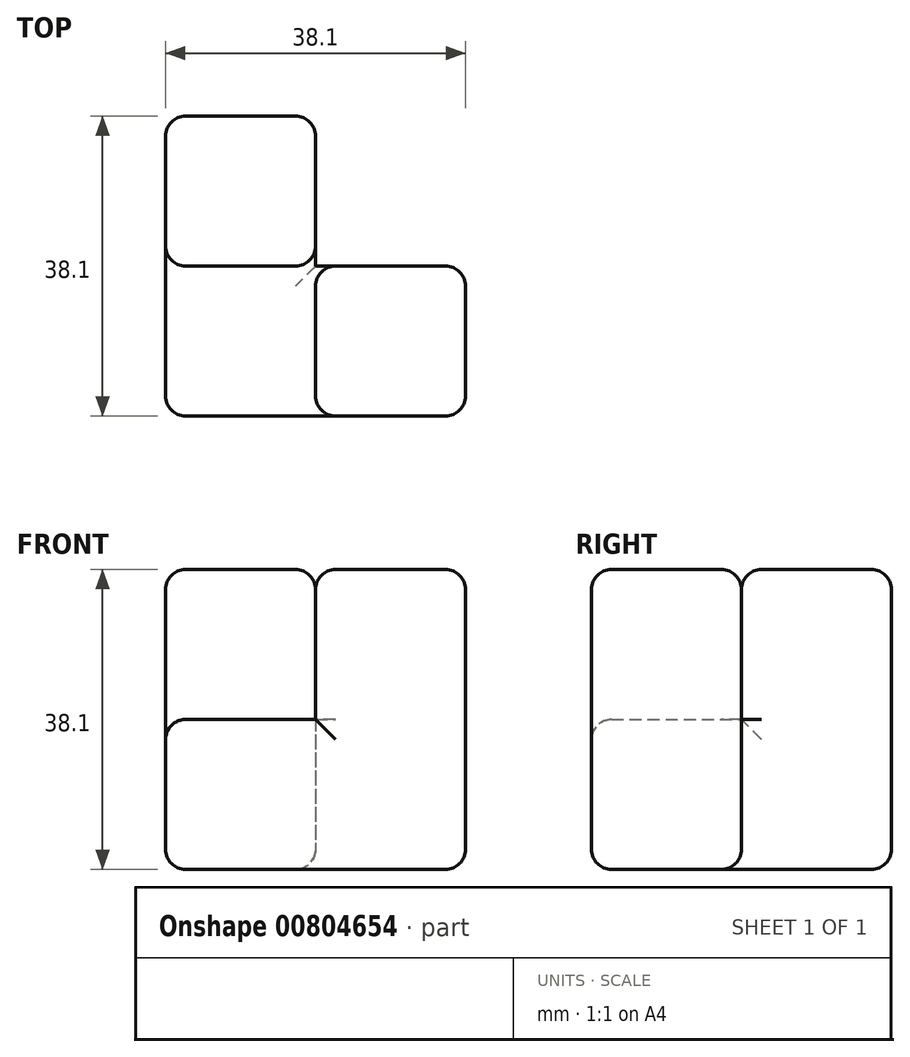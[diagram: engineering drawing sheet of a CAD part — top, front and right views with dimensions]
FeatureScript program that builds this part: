
annotation { "Feature Type Name" : "Feature", "Feature Type Description" : "" }
export const myFeature = defineFeature(function(context is Context, id is Id, definition is map)
    precondition{}
    {
        {
            var Q0;
            Q0=qCreatedBy(makeId("Top.planeOp"),FACE);
            var sketch = newSketch(context, id + "F0", { "sketchPlane" : qUnion([Q0])});
            skLineSegment(sketch, "E0", {"start": v(0, 0) * mm, "end": v(0, 38.1) * mm});
            skLineSegment(sketch, "E1", {"start": v(0, 38.1) * mm, "end": v(19.05, 38.1) * mm});
            skLineSegment(sketch, "E2", {"start": v(19.05, 38.1) * mm, "end": v(19.05, 19.05) * mm});
            skLineSegment(sketch, "E3", {"start": v(19.05, 19.05) * mm, "end": v(38.1, 19.05) * mm});
            skLineSegment(sketch, "E4", {"start": v(38.1, 19.05) * mm, "end": v(38.1, 0) * mm});
            skLineSegment(sketch, "E5", {"start": v(38.1, 0) * mm, "end": v(0, 0) * mm});
            skSolve(sketch);
        }
        {
            var Q0;
            Q0=qSketchRegion(id+"F0",true);
            extrude(context, id + "F1", {"entities" : qUnion([Q0]), "depth" : 19.05 * mm, "offsetDistance" : 25.4 * mm});
        }
        {
            var Q0;
            Q0=makeQuery(id+"F1.opExtrude","CAP_FACE",FACE,{"disambiguationData":[OSD([sQuery(id+"F0.wireOp",EDGE,"E0"),sQuery(id+"F0.wireOp",EDGE,"E1"),sQuery(id+"F0.wireOp",EDGE,"E2"),sQuery(id+"F0.wireOp",EDGE,"E3"),sQuery(id+"F0.wireOp",EDGE,"E4"),sQuery(id+"F0.wireOp",EDGE,"E5")])],"isStart":false});
            var sketch = newSketch(context, id + "F2", { "sketchPlane" : qUnion([Q0])});
            skLineSegment(sketch, "E6.bottom", {"start": v(0, 38.1) * mm, "end": v(19.05, 38.1) * mm});
            skLineSegment(sketch, "E6.top", {"start": v(0, 19.05) * mm, "end": v(19.05, 19.05) * mm});
            skLineSegment(sketch, "E6.left", {"start": v(0, 38.1) * mm, "end": v(0, 19.05) * mm});
            skLineSegment(sketch, "E6.right", {"start": v(19.05, 38.1) * mm, "end": v(19.05, 19.05) * mm});
            skLineSegment(sketch, "E7.bottom", {"start": v(38.1, 0) * mm, "end": v(19.05, 0) * mm});
            skLineSegment(sketch, "E7.top", {"start": v(38.1, 19.05) * mm, "end": v(19.05, 19.05) * mm});
            skLineSegment(sketch, "E7.left", {"start": v(38.1, 0) * mm, "end": v(38.1, 19.05) * mm});
            skLineSegment(sketch, "E7.right", {"start": v(19.05, 0) * mm, "end": v(19.05, 19.05) * mm});
            skSolve(sketch);
        }
        {
            var Q0;
            Q0=makeQuery(id+"F2.imprint","IMPRINT",FACE,{"disambiguationData":[TD([[makeQuery(id+"F2.imprint","IMPRINT",EDGE,{"derivedFrom":sQuery(id+"F2.wireOp",EDGE,"E7.bottom")}),-1.0]])]});
            extrude(context, id + "F3", {"entities" : qUnion([Q0]), "operationType" : NewBodyOperationType.ADD, "depth" : 19.05 * mm, "offsetDistance" : 25.4 * mm});
        }
        {
            var Q0;
            Q0=makeQuery(id+"F3.opExtrude","SWEPT_EDGE",EDGE,{"disambiguationData":[OSD([sQuery(id+"F2.wireOp",EDGE,"E6.top"),sQuery(id+"F2.wireOp",EDGE,"E6.right"),sQuery(id+"F2.wireOp",EDGE,"E7.top"),sQuery(id+"F2.wireOp",EDGE,"E7.right")])]});
            fillet(context, id + "F4", {"entities" : qUnion([Q0]), "radius" : 2.54 * mm, "tangentPropagation" : true, "allowEdgeOverflow" : false});
        }
        {
            var Q0;
            Q0=makeQuery(id+"F2.imprint","IMPRINT",FACE,{"disambiguationData":[TD([[makeQuery(id+"F2.imprint","IMPRINT",EDGE,{"derivedFrom":sQuery(id+"F2.wireOp",EDGE,"E6.bottom")}),-1.0]])]});
            extrude(context, id + "F5", {"entities" : qUnion([Q0]), "operationType" : NewBodyOperationType.ADD, "depth" : 19.05 * mm, "offsetDistance" : 25.4 * mm});
        }
        {
            var Q0;
            Q0=makeQuery(id+"F3.boolean.opBoolean","MERGE",FACE,{"derivedFrom":[makeQuery(id+"F1.opExtrude","SWEPT_FACE",FACE,{"disambiguationData":[OSD([sQuery(id+"F0.wireOp",EDGE,"E4")])]}),makeQuery(id+"F3.opExtrude","SWEPT_FACE",FACE,{"disambiguationData":[OSD([sQuery(id+"F2.wireOp",EDGE,"E7.left")])]})]});
            var Q1;
            Q1=makeQuery(id+"F5.boolean.opBoolean","MERGE",FACE,{"derivedFrom":[makeQuery(id+"F1.opExtrude","SWEPT_FACE",FACE,{"disambiguationData":[OSD([sQuery(id+"F0.wireOp",EDGE,"E1")])]}),makeQuery(id+"F5.opExtrude","SWEPT_FACE",FACE,{"disambiguationData":[OSD([sQuery(id+"F2.wireOp",EDGE,"E6.bottom")])]})]});
            var Q2;
            Q2=makeQuery(id+"F5.opExtrude","CAP_FACE",FACE,{"disambiguationData":[OSD([sQuery(id+"F2.wireOp",EDGE,"E6.bottom"),sQuery(id+"F2.wireOp",EDGE,"E6.top"),sQuery(id+"F2.wireOp",EDGE,"E6.left"),sQuery(id+"F2.wireOp",EDGE,"E6.right")])],"isStart":false});
            var Q3;
            Q3=makeQuery(id+"F3.opExtrude","CAP_FACE",FACE,{"disambiguationData":[OSD([sQuery(id+"F2.wireOp",EDGE,"E7.bottom"),sQuery(id+"F2.wireOp",EDGE,"E7.top"),sQuery(id+"F2.wireOp",EDGE,"E7.left"),sQuery(id+"F2.wireOp",EDGE,"E7.right")])],"isStart":false});
            var Q4;
            Q4=makeQuery(id+"F5.boolean.opBoolean","MERGE",FACE,{"derivedFrom":[makeQuery(id+"F1.opExtrude","SWEPT_FACE",FACE,{"disambiguationData":[OSD([sQuery(id+"F0.wireOp",EDGE,"E0")])]}),makeQuery(id+"F5.opExtrude","SWEPT_FACE",FACE,{"disambiguationData":[OSD([sQuery(id+"F2.wireOp",EDGE,"E6.left")])]})]});
            var Q5;
            Q5=makeQuery(id+"F3.boolean.opBoolean","MERGE",FACE,{"derivedFrom":[makeQuery(id+"F1.opExtrude","SWEPT_FACE",FACE,{"disambiguationData":[OSD([sQuery(id+"F0.wireOp",EDGE,"E5")])]}),makeQuery(id+"F3.opExtrude","SWEPT_FACE",FACE,{"disambiguationData":[OSD([sQuery(id+"F2.wireOp",EDGE,"E7.bottom")])]})]});
            var Q6;
            Q6=makeQuery(id+"F1.opExtrude","CAP_FACE",FACE,{"disambiguationData":[OSD([sQuery(id+"F0.wireOp",EDGE,"E0"),sQuery(id+"F0.wireOp",EDGE,"E1"),sQuery(id+"F0.wireOp",EDGE,"E2"),sQuery(id+"F0.wireOp",EDGE,"E3"),sQuery(id+"F0.wireOp",EDGE,"E4"),sQuery(id+"F0.wireOp",EDGE,"E5")])],"isStart":true});
            var Q7;
            Q7=makeQuery(id+"F5.opExtrude","SWEPT_EDGE",EDGE,{"disambiguationData":[OSD([sQuery(id+"F2.wireOp",EDGE,"E6.top"),sQuery(id+"F2.wireOp",EDGE,"E6.right"),sQuery(id+"F2.wireOp",EDGE,"E7.top"),sQuery(id+"F2.wireOp",EDGE,"E7.right")])]});
            fillet(context, id + "F6", {"entities" : qUnion([Q0, Q1, Q2, Q3, Q4, Q5, Q6, Q7]), "radius" : 2.54 * mm, "tangentPropagation" : true, "allowEdgeOverflow" : false});
        }
    });
